# Revit family: EL_Elektra_L
name_source: partatom
category: Lighting Fixtures
units: mm (PartAtom-declared; Revit-internal decimal feet)

## family parameters
Always vertical = Yes
Cut with Voids When Loaded = No
Light Source = Yes
Maintain Annotation Orientation = No
OmniClass Number = 23.80.70.00
OmniClass Title = Lighting
Part Type = Normal
Room Calculation Point = No
Round Connector Dimension = Use Diameter
Shared = No
Work Plane-Based = No

## types (29) — shared parameters
CE Conformity = CE Mark
Certification = ENEC, ENEC+, EMC, Zhaga D4i, IDA
Color Filter = 16777215
Control Gear = LED Driver
Default Elevation = 1500 mm
Description = Street luminaire
Diffuser Material  = Flat glass
Dimming Lamp Color Temperature Shift = <None>
EL_Voltage = AC 220V - 240V / 50-60Hz
Housing Height = 97 mm
Housing Length = 760 mm
Housing Width = 365 mm  [stored 1.19751 ft]
IK = IK 09 / IK10
IP = IP66
Lamp = LED
Life Time = 120 000 h
Light Source Symbol Length = 3048 mm  [stored 10 ft]
Luminaire Material = Kov
Luminaire Type = ELEKTRA L
Manufacturer = ELEKTRO-LUMEN, s. r. o.
Model = ELEKTRA L
Spot Beam Angle = 30.00°
Spot Field Angle = 90.00°
Terminal Block Poles = 2, 3, 5
Tilt Angle = 90.00°
URL Luminaire = https://www.el-lumen.cz
URL Manufacturer = https://www.el-lumen.cz
Voltage  = AC 220V - 240V / 50-60Hz
Weight = 9.2

## per-type parameters (varying)
| type | CCT | CRI | Luminous Flux of LED | Luminous Flux of Luminaire | Optic | Optical Efficacy | Power |
| ELEKTRA L  Mxx 26k0 740 | 4000 | 70 | 26000 lm | 22768 lm | M03 | 87.57 | 148 W |
| ELEKTRA L  Mxx 24k0 740 | 4000 | 70 | 24000 lm | 21017 lm | M03 | 87.57 | 135 W |
| ELEKTRA L  Mxx 22k0 740 | 4000 | 70 | 22000 lm | 19265 lm | M03 | 87.57 | 130 W |
| ELEKTRA L  Mxx 20k0 740 | 4000 | 70 | 20000 lm | 17514 lm | M03 | 87.57 | 117 W |
| ELEKTRA L  Mxx 18k0 740 | 4000 | 70 | 18000 lm | 15763 lm | M03 | 87.57 | 108 W |
| ELEKTRA L  Mxx 16k0 740 | 4000 | 70 | 16000 lm | 14011 lm | M03 | 87.57 | 94 W |
| ELEKTRA L  Mxx 14k0 740 | 4000 | 70 | 14000 lm | 12260 lm | M03 | 87.57 | 81 W |
| ELEKTRA L  Mxx 26k0 730 | 3000 | 70 | 26000 lm | 22768 lm | M03 | 87.57 | 157 W |
| ELEKTRA L  Mxx 24k0 730 | 3000 | 70 | 24000 lm | 21017 lm | M03 | 87.57 | 143 W |
| ELEKTRA L  Mxx 22k0 730 | 3000 | 70 | 22000 lm | 19265 lm | M03 | 87.57 | 138 W |
| ELEKTRA L  Mxx 20k0 730 | 3000 | 70 | 20000 lm | 17514 lm | M03 | 87.57 | 124 W |
| ELEKTRA L  Mxx 18k0 730 | 3000 | 70 | 18000 lm | 15763 lm | M03 | 87.57 | 116 W |
| ELEKTRA L  Mxx 16k0 730 | 3000 | 70 | 16000 lm | 14011 lm | M03 | 87.57 | 100 W |
| ELEKTRA L  Mxx 14k0 730 | 3000 | 70 | 14000 lm | 12260 lm | M03 | 87.57 | 86 W |
| ELEKTRA L  Mxx 24k0 727 | 2700 | 70 | 24000 lm | 21017 lm | M03 | 87.57 | 150 W |
| ELEKTRA L  Mxx 22k0 727 | 2700 | 70 | 22000 lm | 19265 lm | M03 | 87.57 | 138 W |
| ELEKTRA L  Mxx 20k0 727 | 2700 | 70 | 20000 lm | 17514 lm | M03 | 87.57 | 132 W |
| ELEKTRA L  Mxx 18k0 727 | 2700 | 70 | 18000 lm | 15763 lm | M03 | 87.57 | 117 W |
| ELEKTRA L  Mxx 16k0 727 | 2700 | 70 | 16000 lm | 14011 lm | M03 | 87.57 | 101 W |
| ELEKTRA L  Mxx 14k0 727 | 2700 | 70 | 14000 lm | 12260 lm | M03 | 87.57 | 91 W |
| ELEKTRA L  Mxx 20k0 722 | 2200 | 70 | 20000 lm | 17514 lm | M03 | 87.57 | 143 W |
| ELEKTRA L  Mxx 18k0 722 | 2200 | 70 | 18000 lm | 15763 lm | M03 | 87.57 | 134 W |
| ELEKTRA L  Mxx 16k0 722 | 2200 | 70 | 16000 lm | 14011 lm | M03 | 87.57 | 118 W |
| ELEKTRA L  Mxx 14k0 722 | 2200 | 70 | 14000 lm | 12260 lm | M03 | 87.57 | 101 W |
| ELEKTRA L  Lxx 22k0 AMB | 1850 | 50 | 22000 lm | 19558 lm | L03 | 88.9 | 146 W |
| ELEKTRA L  Lxx 20k0 AMB | 1850 | 50 | 20000 lm | 17780 lm | L03 | 88.9 | 132 W |
| ELEKTRA L  Lxx 18k0 AMB | 1850 | 50 | 18000 lm | 16002 lm | L03 | 88.9 | 122 W |
| ELEKTRA L  Lxx 16k0 AMB | 1850 | 50 | 16000 lm | 14224 lm | L03 | 88.9 | 107 W |
| ELEKTRA L  Lxx 14k0 AMB | 1850 | 50 | 14000 lm | 12446 lm | L03 | 88.9 | 92 W |

note: column(s) folded — value = type name in every type: Luminaire Model

note: [stored X ft] marks values corroborated as IEEE doubles in the binary element streams (Revit-internal decimal feet)
